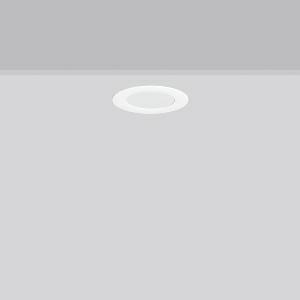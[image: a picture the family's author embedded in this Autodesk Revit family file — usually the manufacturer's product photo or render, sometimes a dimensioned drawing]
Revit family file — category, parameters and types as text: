
# Revit family: toledo_flat_round_e_901452_002_1_583e
name_source: partatom
category: Lighting Fixtures
units: mm (PartAtom-declared; Revit-internal decimal feet)

## family parameters
Cut with Voids When Loaded = No
Host = Face
Light Source = No
Part Type = Normal
Room Calculation Point = No
Round Connector Dimension = Use Diameter
Shared = No

## types (1)
- TOLEDO FLAT round E (1 x LED Modul 840, 840 lm, 4000)
    Apparent Load = 8 VA
    CIE Flux Codes = 47 79 96 100 100
    Color Rendering = 80
    Color Temperature = 4000
    Default Elevation = 1800 mm
    Description = Series: TOLEDO FLAT round
Ultra thin recessed downlight. Housing: die-cast aluminium. Light guide and diffuser made of non-yellowing PMMA, opal matt. Ceiling installation with spring system. Mounting depth depends on ceiling strength. Including separate LED converter with connecting cable 250 mm. Suitable for through-wiring with separately available accessories. Surface mounted housing as accessory for all sizes. Retrofittable decorative cylinders made of chintz fabric as accessory, optional with satin finish plastic diffuser. Through-wiring box (5 pole) available as accessory. 
Colour: white
Diameter: 190 mm
Height: 2.5 mm
Cut-out diameter: 170 mm
Recess height: 27-53 mm
Luminaire: recess height: 31-51 mm
Lamp: LED
Socket: without socket
Colour temperature: 4000K
Colour rendering index (CRI): 80
System power: 7.7 W
Rated luminous flux: 840 lm
Luminous efficiency: 109 lm/W
Control gear: Regulated power supply
Protection class: II
Type of protection: IP 54
    Height = 0 mm  [stored 0 ft]
    Lamp = 1 x LED Modul 840
    Lamp Light Flux = 840 lm
    Lamp count = 1
    Length = 190 mm  [stored 0.62336 ft]
    Lifetime = 50000 h
    Luminous efficacy = 109 lm/W
    Manufacturer = RZB
    ModVariant = No
    Model = 901452.002.1
    Mounting Place = Ceiling
    Mounting Type = Recessed
    Number of Poles = 1
    OnlyDefault = Yes
    Power Factor = 1
    Product Name = TOLEDO FLAT round E
    Product group = Recessed downlights
    ProductGroupID = 402
    Protection Class = Protection class II
    Protection Degree = IP 20
    RLX_Detail_Level = 1
    RLX_Emergency_Light_Flux = 0 lm
    RLX_Emergency_Type = 0
    RLX_Emergency_Type_DB = No
    RlxData = <blob elided: 74429 chars, md5=7ed395fb>
    Socket = socket
    Standby Power = 0 W
    System Light Flux = 840 lm
    System Power = 8 W
    Type Comments = Product without accessories
    Type Image = 901451.002.jpg
    URL = http://relux.com
    VarID = ---
    Voltage = 230 V
    Voltage Range = 220-240 V
    Weight = 0.00 kg
    Width = 0 mm  [stored 0 ft]

note: [stored X ft] marks values corroborated as IEEE doubles in the binary element streams (Revit-internal decimal feet)

## geometry (parser evidence)
native form markers: Blend x4, Sweep x9
no freeform markers — native parametric forms only
